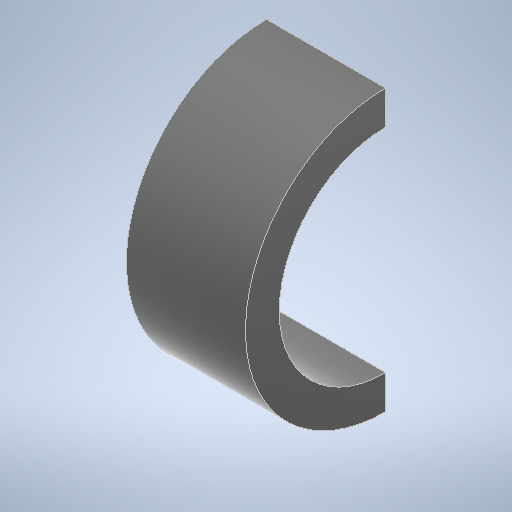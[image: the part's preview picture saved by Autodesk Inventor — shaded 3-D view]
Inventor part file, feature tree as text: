
AUTODESK INVENTOR PART (.ipt)
format: ipt  version: 2025.1 (Build 291241020, 241B)  size: 560,128 bytes
history: native  units: mm
features: sketch x2, revolve x1, extrude x1, projected_geometry x1
ambient origin geometry x8: Origin, YZ Plane, XZ Plane, XY Plane, X Axis, Y Axis, Z Axis, Center Point
bodies: Solid1 (feature_tree)
feature tree (5):
  revolve  "Revolution1"  [1 undecoded]
  extrude  "Extrusion1"  TaperAngle=90.0deg  [1 undecoded]
  sketch  "Sketch1"  dims[d0=6.07mm d1=8.0mm]
  sketch  "Sketch3"  dims[d2=6.8mm d3=90.0deg d4=10.0mm d5=10.0mm d6=0.0mm]
  projected_geometry  "Projected Loop1"
note: 2 required parameter values undecoded (feature->parameter linkage not recoverable at this tier; creation-order binding heuristic only, values carry confidence <= 0.55)